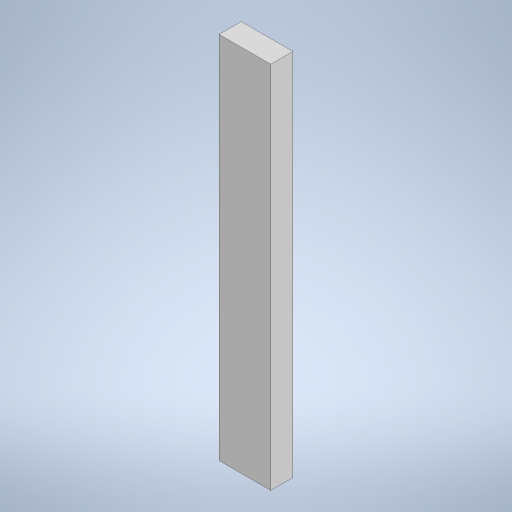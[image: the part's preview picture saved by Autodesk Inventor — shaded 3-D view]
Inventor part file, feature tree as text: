
AUTODESK INVENTOR PART (.ipt)
format: ipt  version: 2023 (Build 270158000, 158)  size: 222,720 bytes
history: native  units: in
note: dims shown in document units (in); Inventor stores cm internally (conversion verified against a paired STEP export)
features: extrude x1, sketch x1
ambient origin geometry x8: Origin, YZ Plane, XZ Plane, XY Plane, X Axis, Y Axis, Z Axis, Center Point
bodies: Solid1 (feature_tree)
feature tree (2):
  extrude  "Extrusion1"  Depth=0.28in
  sketch  "Sketch1"  dims[d0=2.0in d1=0.28in d2=0.12in d3=0.0in]
